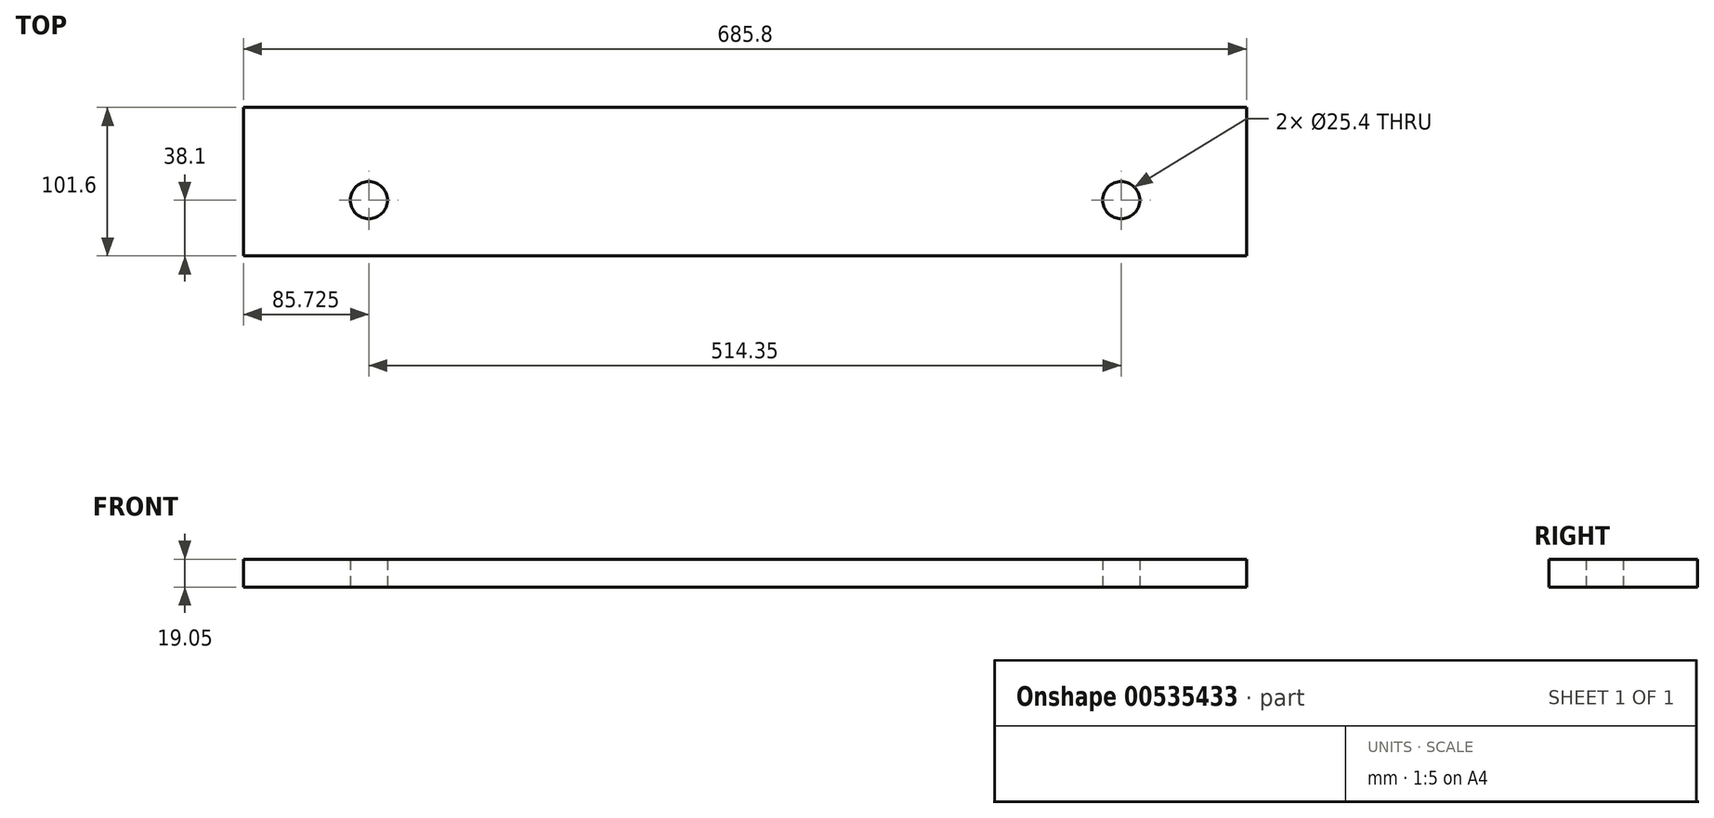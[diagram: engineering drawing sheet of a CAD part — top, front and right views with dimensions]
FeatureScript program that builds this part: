
annotation { "Feature Type Name" : "Feature", "Feature Type Description" : "" }
export const myFeature = defineFeature(function(context is Context, id is Id, definition is map)
    precondition{}
    {
        {
            var Q0;
            Q0=qCreatedBy(makeId("Top.planeOp"),FACE);
            var sketch = newSketch(context, id + "F0", { "sketchPlane" : qUnion([Q0])});
            skLineSegment(sketch, "E0.bottom", {"start": v(342.9, 50.8) * mm, "end": v(-342.9, 50.8) * mm});
            skLineSegment(sketch, "E0.top", {"start": v(342.9, -50.8) * mm, "end": v(-342.9, -50.8) * mm});
            skLineSegment(sketch, "E0.left", {"start": v(342.9, 50.8) * mm, "end": v(342.9, -50.8) * mm});
            skLineSegment(sketch, "E0.right", {"start": v(-342.9, 50.8) * mm, "end": v(-342.9, -50.8) * mm});
            skPoint(sketch, "E0.middle", {"position": v(0, 0) * mm});
            skLineSegment(sketch, "E1.0", {"start": v(342.9, -12.7) * mm, "end": v(-342.9, -12.7) * mm, "construction": true});
            skLineSegment(sketch, "E2", {"start": v(0, -12.7) * mm, "end": v(0, -50.8) * mm, "construction": true});
            skLineSegment(sketch, "E3.0", {"start": v(-257.18, -12.7) * mm, "end": v(-257.18, -50.8) * mm, "construction": true});
            skCircle(sketch, "E4", {"center": v(-257.18, -12.7) * mm, "radius": 12.7 * mm});
            skCircle(sketch, "E5.MirrorC", {"center": v(257.18, -12.7) * mm, "radius": 12.7 * mm});
            skLineSegment(sketch, "E6.MirrorCS", {"start": v(257.18, -12.7) * mm, "end": v(257.18, -50.8) * mm, "construction": true});
            skSolve(sketch);
        }
        {
            var Q0;
            Q0=makeQuery(id+"F0.imprint","IMPRINT",FACE,{"disambiguationData":[TD([[makeQuery(id+"F0.imprint","IMPRINT",EDGE,{"derivedFrom":sQuery(id+"F0.wireOp",EDGE,"E0.bottom")}),1.0]])]});
            extrude(context, id + "F1", {"entities" : qUnion([Q0]), "depth" : 19.05 * mm, "offsetDistance" : 25.4 * mm});
        }
    });
